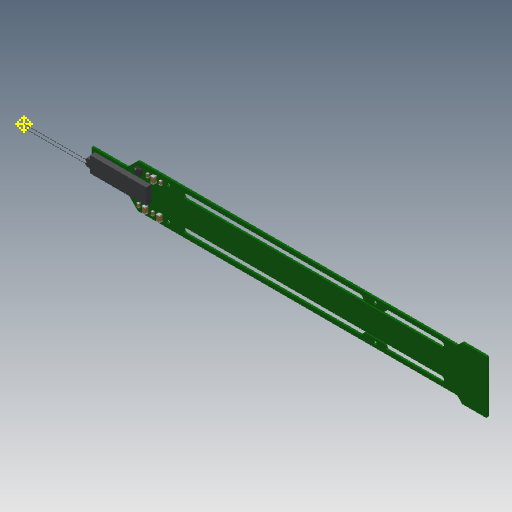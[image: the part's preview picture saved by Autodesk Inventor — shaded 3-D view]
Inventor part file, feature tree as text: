
AUTODESK INVENTOR PART (.ipt)
format: ipt  version: 2020 (Build 240168000, 168)  size: 1,496,576 bytes
history: native  units: in
note: dims shown in document units (in); Inventor stores cm internally (conversion verified against a paired STEP export)
features: other x27, extrude x5, plane x2
ambient origin geometry x8: Origin, YZ Plane, XZ Plane, XY Plane, X Axis, Y Axis, Z Axis, Center Point
bodies: Solid1 (feature_tree), Solid2 (feature_tree), Solid3 (feature_tree), Solid4 (feature_tree), Solid5 (feature_tree), Solid6 (feature_tree), Solid7 (feature_tree), Solid8 (feature_tree), Solid9 (feature_tree), Solid10 (feature_tree), Solid11 (feature_tree), Solid12 (feature_tree), Solid13 (feature_tree), Solid14 (feature_tree), Solid15 (feature_tree), Solid16 (feature_tree), Solid17 (feature_tree), Solid18 (feature_tree), Solid19 (feature_tree), Solid20 (feature_tree), Solid21 (feature_tree), Solid22 (feature_tree), Solid23 (feature_tree), Solid24 (feature_tree), Solid25 (feature_tree), Solid26 (feature_tree), Solid27 (feature_tree), Solid28 (feature_tree), Solid29 (feature_tree), Solid30 (feature_tree), Solid31 (feature_tree)
feature tree (34):
  other  "Work Point2- probe center"
  plane  "Work Plane1"
  plane  "Work Plane2"
  other  "Board_1:1"
  other  "CerCap_0402_2:1"
  other  "CerCap_0402_2:2"
  other  "CerCap_0402_2:3"
  extrude  "Extruded_4:1"  [1 undecoded]
  extrude  "Extruded_6:1"  Depth=0.03in
  extrude  "Extruded_6:2"  [1 undecoded]
  other  "Sphere_10:1"
  other  "Sphere_10:2"
  other  "Sphere_10:3"
  other  "Sphere_10:4"
  extrude  "Extruded_15:1"  [1 undecoded]
  extrude  "Extruded_17:1"  [1 undecoded]
  other  "CerCap_0201_20:1"
  other  "CerCap_0201_20:2"
  other  "CerCap_0201_20:3"
  other  "CerCap_0201_22:1"
  other  "CerCap_0201_22:2"
  other  "CerCap_0201_22:3"
  other  "CerCap_0402_24:1"
  other  "CerCap_0402_24:2"
  other  "CerCap_0402_24:3"
  other  "CerCap_0201_26:1"
  other  "CerCap_0201_26:2"
  other  "CerCap_0201_26:3"
  other  "CerCap_0402_28:1"
  other  "CerCap_0402_28:2"
  other  "CerCap_0402_28:3"
  other  "CerCap_0201_30:1"
  other  "CerCap_0201_30:2"
  other  "CerCap_0201_30:3"
note: 4 required parameter values undecoded (feature->parameter linkage not recoverable at this tier; creation-order binding heuristic only, values carry confidence <= 0.55)
